# Revit family: Hekatron_Feststellanlagen_ORS 142 W si_DE_22.01
name_source: partatom
category: Brandmelder
revit_build: Autodesk Revit 2018 (Build: 20190510_1515(x64)
units: mm (PartAtom-declared; Revit-internal decimal feet)

## family parameters
Basisbauteil = Fläche
Beim Laden mit Abzugskörper schneiden = Nein
Bemaßung runder Anschluss = Durchmesser verwenden
Beschriftungsausrichtung beibehalten = Ja
Gemeinsam genutzt = Nein
OmniClass-Nummer = 23.85.30.21
OmniClass-Titel = Environmental Detection/Registration
Raumberechnungspunkt = Nein
Teiletyp = Normal

## types (1)
- ORS 142 W si
    Ansprechtemperatur = 70.0
    Bauartgenehmigungen = Z-6.500-2405, Z-6.500-2401, Z-6.500-2396, Z-6.500-2382, Z-6.500-2363, Z-6.500-2359, Z-6.500-2393, Z-6.500-2394, Z-6.500-2414, Z-6.500-2415, Z-6.500-2381, Z-6.500-2422, Z-6.500-2298, Z-6.500-2365, Z-6.500-2403, Z-6.500-2419, Z-6.500-2441, Z-6.500-2434, Z-6.500-2432, Z-6.500-2413, Z-6.500-2442, Z-6.500-2400, Z-6.500-2446, Z-6.500-2436, Z-6.500-2449, Z-6.500-2451, Z-6.500-2452, Z-6.500-2499, Z-6.500-2509
    Beschreibung = Optischer Rauchschalter für Wand- oder Sturzmontage zum Einsatz in Feststellanlagen und weiteren Anwendungen.
    Betriebsspannung = 18 bis 28 V DC
    Breite (mm) = 127.0
    Farbe = silber, ähnlich RAL 9006
    Funktionsprinzip = optisch
    Hersteller = Hekatron
    Höhe (mm) = 35.0
    Kabeleinführung = hinten, seitlich
    Link zu Ausschreibungstext = https://www.meinhplus.de
    Link zu ausschreiben.de = http://www.ausschreiben.de
    Material = PC
    Modell = ORS 142 W si
    Montageart = Wand- oder Sturzmontage
    Nettogewicht (g) = 130.0
    Schutzart = IP 40
    Stromaufnahme = max. 25mA
    Tiefe (mm) = 36.0
    Typenkommentare = Rauchschalter ORS 142 W in silber
    UB A&S Artikel Nummer = 31-5000033-02-01
    URL = https://www.hekatron-brandschutz.de
    Version des BIM Objektes = 22.01
    Vorgabe-Ansicht = 1200 mm
    Zulässige Umgebungstemperatur = -20 °C bis +75 °C

## geometry (parser evidence)
native form markers: Extrusion x1, Sweep x2
no freeform markers — native parametric forms only
